# Revit family: NBS_GreshamOfficeFurnitureLtd_OffcChrs_ReloSwivel
name_source: partatom
category: Furniture
units: mm (PartAtom-declared; Revit-internal decimal feet)

## family parameters
Always vertical = Yes
Cut with Voids When Loaded = No
Room Calculation Point = No
Shared = No
Work Plane-Based = No

## types (2) — shared parameters
AssetType = Fixed
BaseColour = Black, White, Grey, Silver, Bronze
Category = Pr_40_50_12_57:Office chairs
DurationUnit = year
FrameColour = Manufacturer's standard
FrameFinish = Manufacturer's standard
FrameMaterial = Metal internal frame
IfcExportAs = IfcFurnitureType
IfcExportType = CHAIR
Manufacturer = Contact Us – Gresham Office Furniture (gof.co.uk)
ManufacturerName = Gresham Office Furniture Ltd
ManufacturerURL = www.gof.co.uk
NBSCertification = www.nationalbimlibrary.com/cert/nv2gho4q
Recyclability = 100%
StandardsDurability = To BS EN 16139:2013
Uniclass2015Code = Pr_40_50_12_57
Uniclass2015Title = Office chairs
Uniclass2015Version = Products v1.22
Version = 1
WarrantyDurationUnit = year
zero-valued in all types: NominalHeight, NominalLength, NominalWidth

## per-type parameters (varying)
| type | BIMObjectName | BaseType | Name | SeatsAndBacksColour | SeatsAndBacksMaterial |
| RELOSW1 - Upholstered Shroud with Swivel Base | NBS_GreshamOfficeFurnitureLtd_OfficeChairs_ReloSwivel_RELOSW1UpholsteredShroudwithSwivelBase | Static | OfficeChairs_Relo_RELOSW1_UpholsteredShroudwithSwivelBase_GreshamOfficeFurnitureLtd |  | Moulded polyurethane foam/ fabric |
| RELOSW2 - TECH® PU Shroud with Swivel Base | NBS_GreshamOfficeFurnitureLtd_OfficeChairs_ReloSwivel_RELOSW2TECHPUShroudwithSwivelBase | Swivel | OfficeChairs_Relo_RELOSW2_TECH_PU_ShroudwithSwivelBase_GreshamOfficeFurnitureLtd | Fabric/ Powder White outer shroud, Fabric/ Simply Taupe outer shroud, Fabric/ Charleston Grey outer shroud, Fabric/ Babouche Yellow outer shroud, Fabric/ Yearbridge Green outer shroud, Fabric/ custom colour outer shroud | Moulded polyurethane foam/ fabric/ TECH® PU |

note: column(s) folded — value = type name in every type: ModelReference

## geometry (parser evidence)
native form markers: Sweep x2
no freeform markers — native parametric forms only
